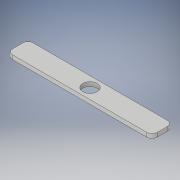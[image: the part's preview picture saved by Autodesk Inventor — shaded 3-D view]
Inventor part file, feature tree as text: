
AUTODESK INVENTOR PART (.ipt)
format: ipt  version: 2018 (Build 220112000, 112)  size: 110,592 bytes
history: native  units: in
note: dims shown in document units (in); Inventor stores cm internally (conversion verified against a paired STEP export)
features: extrude x2, sketch x2, fillet x1
ambient origin geometry x8: Origin, YZ Plane, XZ Plane, XY Plane, X Axis, Y Axis, Z Axis, Center Point
bodies: Solid1 (feature_tree)
feature tree (5):
  extrude  "Extrusion1"  Depth=0.5in
  fillet  "Fillet1"  Radius=0.1in
  extrude  "Extrusion2"  Depth=0.1in
  sketch  "Sketch1"  dims[d0=3.5in d1=0.5in d2=0.1in d3=0.0in]
  sketch  "Sketch2"  dims[d4=0.125in d5=1.75in d6=0.35in d7=0.1in d8=0.0in]
